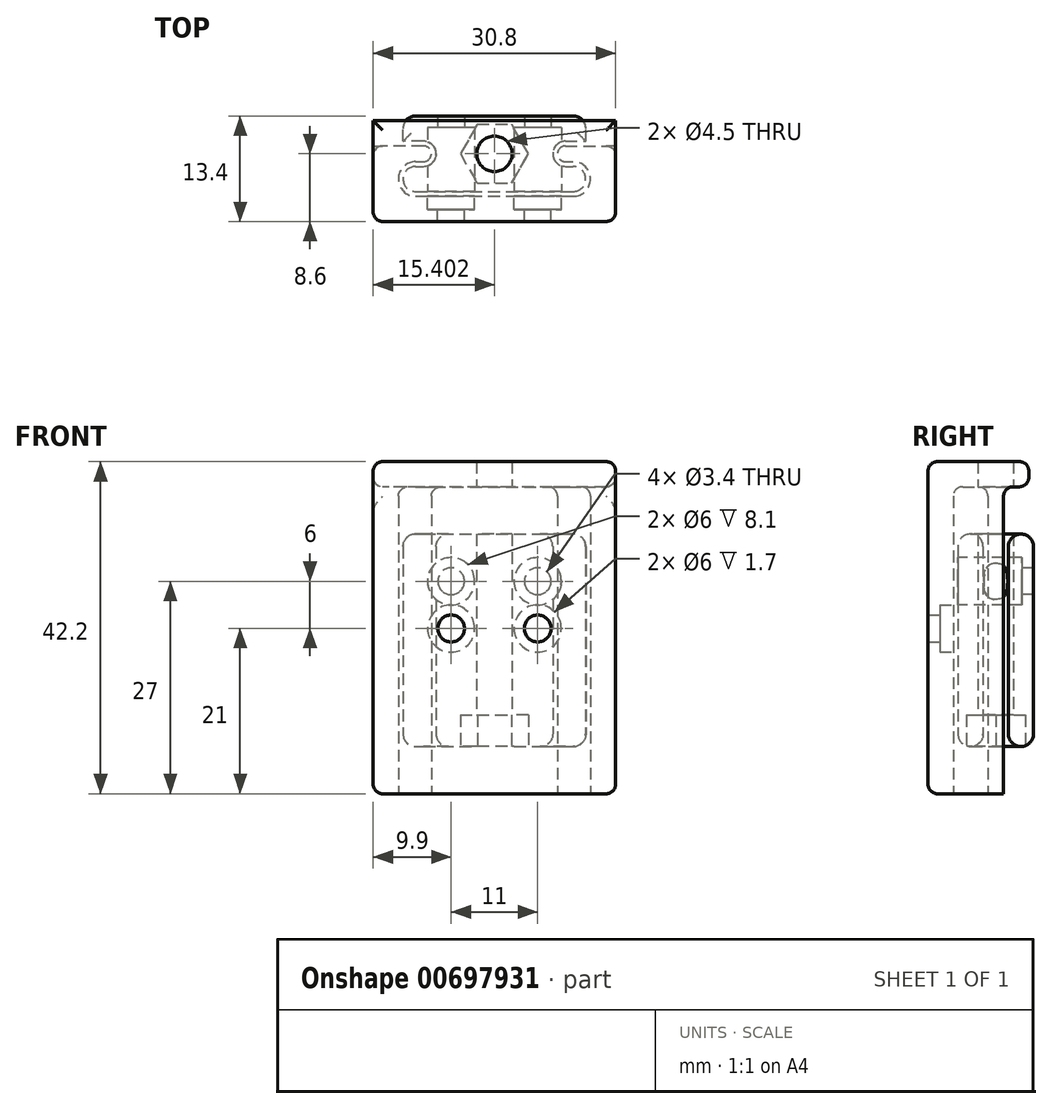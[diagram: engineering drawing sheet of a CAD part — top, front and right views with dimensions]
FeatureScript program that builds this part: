
annotation { "Feature Type Name" : "Feature", "Feature Type Description" : "" }
export const myFeature = defineFeature(function(context is Context, id is Id, definition is map)
    precondition{}
    {
        {
            assignVariable(context, id + "F0", {"name" : "HoleWallD", "anyValue" : 1.5});
        }
        {
            assignVariable(context, id + "F1", {"name" : "RailD", "anyValue" : 3.2});
        }
        {
            assignVariable(context, id + "F2", {"name" : "SliderH", "anyValue" : 21 + 6});
        }
        {
            assignVariable(context, id + "F3", {"name" : "SliderBoltHole", "anyValue" : 4.5});
        }
        {
            assignVariable(context, id + "F4", {"name" : "MountH", "anyValue" : 21 + 6 + 12});
        }
        {
            var Q0;
            Q0=qCreatedBy(makeId("Top.planeOp"),FACE);
            var sketch = newSketch(context, id + "F5", { "sketchPlane" : qUnion([Q0])});
            skArc(sketch, "E0", {"start": v(-9, -0.47) * mm, "mid": v(-7.4, 1.13) * mm, "end": v(-9, 2.73) * mm});
            skLineSegment(sketch, "E1", {"start": v(-9, 2.73) * mm, "end": v(-11.6, 2.73) * mm});
            skLineSegment(sketch, "E2", {"start": v(-11.6, 2.73) * mm, "end": v(-11.6, 5.93) * mm});
            skLineSegment(sketch, "E3", {"start": v(-10, -3.67) * mm, "end": v(0, -3.67) * mm});
            skLineSegment(sketch, "E4", {"start": v(0, 5.93) * mm, "end": v(-11.6, 5.93) * mm});
            skLineSegment(sketch, "E5", {"start": v(-15.4, -7.47) * mm, "end": v(0, -7.47) * mm});
            skLineSegment(sketch, "E6", {"start": v(-10, -0.47) * mm, "end": v(-9, -0.47) * mm});
            skPoint(sketch, "E7", {"position": v(-5.5, 5.93) * mm});
            skPoint(sketch, "E8", {"position": v(-5.5, -7.47) * mm});
            skArc(sketch, "E9", {"start": v(-10, -0.47) * mm, "mid": v(-11.6, -2.07) * mm, "end": v(-10, -3.67) * mm});
            skLineSegment(sketch, "E10.0", {"start": v(-10, -4.27) * mm, "end": v(0, -4.27) * mm});
            skLineSegment(sketch, "E10.1", {"start": v(-9, 2.13) * mm, "end": v(-15.4, 2.13) * mm});
            skArc(sketch, "E10.2", {"start": v(-9, 0.13) * mm, "mid": v(-8, 1.13) * mm, "end": v(-9, 2.13) * mm});
            skLineSegment(sketch, "E10.3", {"start": v(-10, 0.13) * mm, "end": v(-9, 0.13) * mm});
            skArc(sketch, "E10.4", {"start": v(-10, 0.13) * mm, "mid": v(-12.2, -2.07) * mm, "end": v(-10, -4.27) * mm});
            skLineSegment(sketch, "E11", {"start": v(-15.4, 2.13) * mm, "end": v(-15.4, -7.47) * mm});
            skLineSegment(sketch, "E12", {"start": v(0, 5.93) * mm, "end": v(0, 5.93) * mm});
            skLineSegment(sketch, "E13", {"start": v(0, -4.27) * mm, "end": v(0, -7.47) * mm});
            skLineSegment(sketch, "E14.MirrorCS", {"start": v(10, -4.27) * mm, "end": v(0, -4.27) * mm});
            skLineSegment(sketch, "E15.MirrorCS", {"start": v(10, -3.67) * mm, "end": v(0, -3.67) * mm});
            skArc(sketch, "E16.MirrorCS", {"start": v(9, -0.47) * mm, "mid": v(7.4, 1.13) * mm, "end": v(9, 2.73) * mm});
            skLineSegment(sketch, "E17.MirrorCS", {"start": v(9, 2.13) * mm, "end": v(15.4, 2.13) * mm});
            skPoint(sketch, "E18.MirrorP", {"position": v(5.5, 5.93) * mm});
            skLineSegment(sketch, "E19.MirrorCS", {"start": v(15.4, -7.47) * mm, "end": v(0, -7.47) * mm});
            skArc(sketch, "E20.MirrorCS", {"start": v(9, 0.13) * mm, "mid": v(8, 1.13) * mm, "end": v(9, 2.13) * mm});
            skLineSegment(sketch, "E21.MirrorCS", {"start": v(9, 2.73) * mm, "end": v(11.6, 2.73) * mm});
            skLineSegment(sketch, "E22.MirrorCS", {"start": v(9, 0.13) * mm, "end": v(10, 0.13) * mm});
            skLineSegment(sketch, "E23.MirrorCS", {"start": v(0, 5.93) * mm, "end": v(11.6, 5.93) * mm});
            skArc(sketch, "E24.MirrorCS", {"start": v(10, 0.13) * mm, "mid": v(12.2, -2.07) * mm, "end": v(10, -4.27) * mm});
            skLineSegment(sketch, "E25.MirrorCS", {"start": v(11.6, 2.73) * mm, "end": v(11.6, 5.93) * mm});
            skArc(sketch, "E26.MirrorCS", {"start": v(10, -0.47) * mm, "mid": v(11.6, -2.07) * mm, "end": v(10, -3.67) * mm});
            skLineSegment(sketch, "E27.MirrorCS", {"start": v(9, -0.47) * mm, "end": v(10, -0.47) * mm});
            skLineSegment(sketch, "E28.MirrorCS", {"start": v(15.4, 2.13) * mm, "end": v(15.4, -7.47) * mm});
            skPoint(sketch, "E29.MirrorP", {"position": v(5.5, -7.47) * mm});
            skSolve(sketch);
        }
        {
            var Q0;
            Q0=makeQuery(id+"F5.imprint","IMPRINT",FACE,{"disambiguationData":[TD([[makeQuery(id+"F5.imprint","IMPRINT",EDGE,{"derivedFrom":sQuery(id+"F5.wireOp",EDGE,"E0")}),-1.0]])]});
            var Q1;
            {var subQ1=sQuery(id+"F5.wireOp",EDGE,"E15.MirrorCS");Q1=makeQuery(id+"F5.imprint","IMPRINT",FACE,{"disambiguationData":[TD([[makeQuery(id+"F5.imprint","IMPRINT",EDGE,{"derivedFrom":subQ1}),-1.0]])]});}
            extrude(context, id + "F6", {"entities" : qUnion([Q0, Q1]), "endBound" : BoundingType.SYMMETRIC, "depth" : (getVariable(context, 'SliderH')) * mm, "offsetDistance" : 25 * mm});
        }
        {
            var Q0;
            Q0=makeQuery(id+"F6.opExtrude","SWEPT_EDGE",EDGE,{"disambiguationData":[OSD([sQuery(id+"F5.wireOp",EDGE,"E2"),sQuery(id+"F5.wireOp",EDGE,"E4")])]});
            var Q1;
            Q1=makeQuery(id+"F6.opExtrude","SWEPT_EDGE",EDGE,{"disambiguationData":[OSD([sQuery(id+"F5.wireOp",EDGE,"E23.MirrorCS"),sQuery(id+"F5.wireOp",EDGE,"E25.MirrorCS")])]});
            var Q2;
            Q2=makeQuery(id+"F6.opExtrude","CAP_FACE",FACE,{"disambiguationData":[OSD([sQuery(id+"F5.wireOp",EDGE,"E0"),sQuery(id+"F5.wireOp",EDGE,"E1"),sQuery(id+"F5.wireOp",EDGE,"E2"),sQuery(id+"F5.wireOp",EDGE,"E3"),sQuery(id+"F5.wireOp",EDGE,"E4"),sQuery(id+"F5.wireOp",EDGE,"E6"),sQuery(id+"F5.wireOp",EDGE,"E9"),sQuery(id+"F5.wireOp",EDGE,"E15.MirrorCS"),sQuery(id+"F5.wireOp",EDGE,"E16.MirrorCS"),sQuery(id+"F5.wireOp",EDGE,"E21.MirrorCS"),sQuery(id+"F5.wireOp",EDGE,"E23.MirrorCS"),sQuery(id+"F5.wireOp",EDGE,"E25.MirrorCS"),sQuery(id+"F5.wireOp",EDGE,"E26.MirrorCS"),sQuery(id+"F5.wireOp",EDGE,"E27.MirrorCS")])],"isStart":true});
            var Q3;
            Q3=makeQuery(id+"F6.opExtrude","CAP_FACE",FACE,{"disambiguationData":[OSD([sQuery(id+"F5.wireOp",EDGE,"E0"),sQuery(id+"F5.wireOp",EDGE,"E1"),sQuery(id+"F5.wireOp",EDGE,"E2"),sQuery(id+"F5.wireOp",EDGE,"E3"),sQuery(id+"F5.wireOp",EDGE,"E4"),sQuery(id+"F5.wireOp",EDGE,"E6"),sQuery(id+"F5.wireOp",EDGE,"E9"),sQuery(id+"F5.wireOp",EDGE,"E15.MirrorCS"),sQuery(id+"F5.wireOp",EDGE,"E16.MirrorCS"),sQuery(id+"F5.wireOp",EDGE,"E21.MirrorCS"),sQuery(id+"F5.wireOp",EDGE,"E23.MirrorCS"),sQuery(id+"F5.wireOp",EDGE,"E25.MirrorCS"),sQuery(id+"F5.wireOp",EDGE,"E26.MirrorCS"),sQuery(id+"F5.wireOp",EDGE,"E27.MirrorCS")])],"isStart":false});
            fillet(context, id + "F7", {"entities" : qUnion([Q0, Q1, Q2, Q3]), "radius" : 1.6 * mm, "tangentPropagation" : true, "allowEdgeOverflow" : false});
        }
        {
            var Q0;
            Q0=makeQuery(id+"F6.opExtrude","SWEPT_FACE",FACE,{"disambiguationData":[OSD([sQuery(id+"F5.wireOp",EDGE,"E3"),sQuery(id+"F5.wireOp",EDGE,"E15.MirrorCS")])]});
            var sketch = newSketch(context, id + "F8", { "sketchPlane" : qUnion([Q0])});
            skLineSegment(sketch, "E30.bottom", {"start": v(5.5, 7.5) * mm, "end": v(-5.5, 7.5) * mm});
            skLineSegment(sketch, "E30.top", {"start": v(5.5, -7.5) * mm, "end": v(-5.5, -7.5) * mm});
            skLineSegment(sketch, "E30.left", {"start": v(5.5, 7.5) * mm, "end": v(5.5, -7.5) * mm});
            skLineSegment(sketch, "E30.right", {"start": v(-5.5, 7.5) * mm, "end": v(-5.5, -7.5) * mm});
            skPoint(sketch, "E30.middle", {"position": v(0, 0) * mm});
            skSolve(sketch);
        }
        {
            var Q0;
            Q0=makeQuery(id+"F6.opExtrude","CAP_FACE",FACE,{"disambiguationData":[OSD([sQuery(id+"F5.wireOp",EDGE,"E0"),sQuery(id+"F5.wireOp",EDGE,"E1"),sQuery(id+"F5.wireOp",EDGE,"E2"),sQuery(id+"F5.wireOp",EDGE,"E3"),sQuery(id+"F5.wireOp",EDGE,"E4"),sQuery(id+"F5.wireOp",EDGE,"E6"),sQuery(id+"F5.wireOp",EDGE,"E9"),sQuery(id+"F5.wireOp",EDGE,"E12"),sQuery(id+"F5.wireOp",EDGE,"E15.MirrorCS"),sQuery(id+"F5.wireOp",EDGE,"E16.MirrorCS"),sQuery(id+"F5.wireOp",EDGE,"E12"),sQuery(id+"F5.wireOp",EDGE,"E21.MirrorCS"),sQuery(id+"F5.wireOp",EDGE,"E23.MirrorCS"),sQuery(id+"F5.wireOp",EDGE,"E25.MirrorCS"),sQuery(id+"F5.wireOp",EDGE,"E26.MirrorCS"),sQuery(id+"F5.wireOp",EDGE,"E27.MirrorCS")])],"isStart":true});
            var sketch = newSketch(context, id + "F9", { "sketchPlane" : qUnion([Q0])});
            skPoint(sketch, "E31", {"position": v(0, 0) * mm});
            skCircle(sketch, "E32.cCircle", {"center": v(0, -1.13) * mm, "radius": 3.75 * mm, "construction": true});
            skLineSegment(sketch, "E32.0", {"start": v(4.33, -1.13) * mm, "end": v(2.17, -4.88) * mm});
            skLineSegment(sketch, "E32.1", {"start": v(2.17, -4.88) * mm, "end": v(-2.16, -4.88) * mm});
            skLineSegment(sketch, "E32.2", {"start": v(-2.16, -4.88) * mm, "end": v(-4.33, -1.13) * mm});
            skLineSegment(sketch, "E32.3", {"start": v(-4.33, -1.13) * mm, "end": v(-2.16, 2.62) * mm});
            skLineSegment(sketch, "E32.4", {"start": v(-2.16, 2.62) * mm, "end": v(2.17, 2.62) * mm});
            skLineSegment(sketch, "E32.5", {"start": v(2.17, 2.62) * mm, "end": v(4.33, -1.13) * mm});
            skPoint(sketch, "E32.0.midPoint", {"position": v(3.25, -3) * mm});
            skSolve(sketch);
        }
        {
            var Q0;
            Q0=sQuery(id+"F8.wireOp",VERTEX,"E30.right.start");
            var Q1;
            Q1=sQuery(id+"F8.wireOp",VERTEX,"E30.left.start");
            var Q2;
            Q2=makeQuery(id+"F6.opExtrude","SWEPT_BODY",BODY,{"disambiguationData":[OSD([sQuery(id+"F5.wireOp",EDGE,"E0"),sQuery(id+"F5.wireOp",EDGE,"E1"),sQuery(id+"F5.wireOp",EDGE,"E2"),sQuery(id+"F5.wireOp",EDGE,"E3"),sQuery(id+"F5.wireOp",EDGE,"E4"),sQuery(id+"F5.wireOp",EDGE,"E6"),sQuery(id+"F5.wireOp",EDGE,"E9"),sQuery(id+"F5.wireOp",EDGE,"E12"),sQuery(id+"F5.wireOp",EDGE,"E15.MirrorCS"),sQuery(id+"F5.wireOp",EDGE,"E16.MirrorCS"),sQuery(id+"F5.wireOp",EDGE,"E12"),sQuery(id+"F5.wireOp",EDGE,"E21.MirrorCS"),sQuery(id+"F5.wireOp",EDGE,"E23.MirrorCS"),sQuery(id+"F5.wireOp",EDGE,"E25.MirrorCS"),sQuery(id+"F5.wireOp",EDGE,"E26.MirrorCS"),sQuery(id+"F5.wireOp",EDGE,"E27.MirrorCS")])]});
            hole(context, id + "F10", {"style" : HoleStyle.C_BORE, "endStyle" : HoleEndStyle.THROUGH, "holeDiameter" : 3.4 * mm, "cBoreDiameter" : 6 * mm, "cBoreDepth" : ((getVariable(context, 'RailD') * 3) - getVariable(context, 'HoleWallD')) * mm, "majorDiameter" : 5 * mm, "isTappedThrough" : true, "tappedDepth" : 12 * mm, "tapClearance" : 3, "locations" : qUnion([Q0, Q1]), "scope" : qUnion([Q2])});
        }
        {
            var Q0;
            {var subQ4=sQuery(id+"F9.wireOp",EDGE,"E32.2");Q0=makeQuery(id+"F9.imprint","IMPRINT",FACE,{"disambiguationData":[TD([[makeQuery(id+"F9.imprint","IMPRINT",EDGE,{"derivedFrom":subQ4}),-1.0]])]});}
            var Q1;
            {var subQ5=sQuery(id+"F9.wireOp",EDGE,"E32.0");Q1=makeQuery(id+"F9.imprint","IMPRINT",FACE,{"disambiguationData":[TD([[makeQuery(id+"F9.imprint","IMPRINT",EDGE,{"derivedFrom":subQ5}),-1.0]])]});}
            var Q2;
            {var subQ0=sQuery(id+"F9.wireOp",EDGE,"E32.4");Q2=makeQuery(id+"F9.imprint","IMPRINT",FACE,{"disambiguationData":[TD([[makeQuery(id+"F9.imprint","IMPRINT",EDGE,{"derivedFrom":subQ0}),-1.0]])]});}
            var Q3;
            {var subQ0=sQuery(id+"F9.wireOp",EDGE,"E32.5");var subQ1=sQuery(id+"F9.wireOp",EDGE,"E32.0");var subQ2=makeQuery(id+"F9.imprint","INTERSECT",VERTEX,{"derivedFrom":[subQ1,subQ0]});Q3=makeQuery(id+"F9.imprint","IMPRINT",FACE,{"disambiguationData":[TD([[makeQuery(id+"F9.imprint","IMPRINT",EDGE,{"disambiguationData":[TD([[subQ2,-1.0]])],"derivedFrom":subQ1}),-1.0]])]});}
            extrude(context, id + "F11", {"entities" : qUnion([Q0, Q1, Q2, Q3]), "operationType" : NewBodyOperationType.REMOVE, "oppositeDirection" : true, "depth" : 4 * mm, "offsetDistance" : 25 * mm});
        }
        {
            var Q0;
            Q0=sQuery(id+"F9.wireOp",VERTEX,"E32.cCircle.center");
            var Q1;
            Q1=makeQuery(id+"F6.opExtrude","SWEPT_BODY",BODY,{"disambiguationData":[OSD([sQuery(id+"F5.wireOp",EDGE,"E0"),sQuery(id+"F5.wireOp",EDGE,"E1"),sQuery(id+"F5.wireOp",EDGE,"E2"),sQuery(id+"F5.wireOp",EDGE,"E3"),sQuery(id+"F5.wireOp",EDGE,"E4"),sQuery(id+"F5.wireOp",EDGE,"E6"),sQuery(id+"F5.wireOp",EDGE,"E9"),sQuery(id+"F5.wireOp",EDGE,"E12"),sQuery(id+"F5.wireOp",EDGE,"E15.MirrorCS"),sQuery(id+"F5.wireOp",EDGE,"E16.MirrorCS"),sQuery(id+"F5.wireOp",EDGE,"E12"),sQuery(id+"F5.wireOp",EDGE,"E21.MirrorCS"),sQuery(id+"F5.wireOp",EDGE,"E23.MirrorCS"),sQuery(id+"F5.wireOp",EDGE,"E25.MirrorCS"),sQuery(id+"F5.wireOp",EDGE,"E26.MirrorCS"),sQuery(id+"F5.wireOp",EDGE,"E27.MirrorCS")])]});
            hole(context, id + "F12", {"style" : HoleStyle.SIMPLE, "endStyle" : HoleEndStyle.THROUGH, "holeDiameter" : (getVariable(context, 'SliderBoltHole')) * mm, "majorDiameter" : 5 * mm, "isTappedThrough" : true, "tappedDepth" : 12 * mm, "tapClearance" : 3, "locations" : qUnion([Q0]), "scope" : qUnion([Q1])});
        }
        {
            var Q0;
            Q0=makeQuery(id+"F5.imprint","IMPRINT",FACE,{"disambiguationData":[TD([[makeQuery(id+"F5.imprint","IMPRINT",EDGE,{"derivedFrom":sQuery(id+"F5.wireOp",EDGE,"E5")}),1.0]])]});
            var Q1;
            Q1=makeQuery(id+"F5.imprint","IMPRINT",FACE,{"disambiguationData":[TD([[makeQuery(id+"F5.imprint","IMPRINT",EDGE,{"derivedFrom":sQuery(id+"F5.wireOp",EDGE,"E14.MirrorCS")}),1.0]])]});
            extrude(context, id + "F13", {"entities" : qUnion([Q0, Q1]), "endBound" : BoundingType.SYMMETRIC, "depth" : (getVariable(context, 'MountH')) * mm, "offsetDistance" : 25 * mm});
        }
        {
            var Q0;
            Q0=makeQuery(id+"F13.opExtrude","SWEPT_FACE",FACE,{"disambiguationData":[OSD([sQuery(id+"F5.wireOp",EDGE,"E10.0"),sQuery(id+"F5.wireOp",EDGE,"E14.MirrorCS")])]});
            var sketch = newSketch(context, id + "F14", { "sketchPlane" : qUnion([Q0])});
            skLineSegment(sketch, "E33.bottom", {"start": v(-5.5, 1.5) * mm, "end": v(5.5, 1.5) * mm});
            skLineSegment(sketch, "E33.top", {"start": v(5.5, -1.5) * mm, "end": v(-5.5, -1.5) * mm});
            skLineSegment(sketch, "E33.left", {"start": v(-5.5, 1.5) * mm, "end": v(-5.5, -1.5) * mm});
            skLineSegment(sketch, "E33.right", {"start": v(5.5, 1.5) * mm, "end": v(5.5, -1.5) * mm});
            skPoint(sketch, "E33.middle", {"position": v(0, 0) * mm});
            skSolve(sketch);
        }
        {
            var Q0;
            Q0=sQuery(id+"F14.wireOp",VERTEX,"E33.bottom.start");
            var Q1;
            Q1=sQuery(id+"F14.wireOp",VERTEX,"E33.right.start");
            var Q2;
            Q2=makeQuery(id+"F13.opExtrude","SWEPT_BODY",BODY,{"disambiguationData":[OSD([sQuery(id+"F5.wireOp",EDGE,"E5"),sQuery(id+"F5.wireOp",EDGE,"E10.0"),sQuery(id+"F5.wireOp",EDGE,"E10.1"),sQuery(id+"F5.wireOp",EDGE,"E10.2"),sQuery(id+"F5.wireOp",EDGE,"E10.3"),sQuery(id+"F5.wireOp",EDGE,"E10.4"),sQuery(id+"F5.wireOp",EDGE,"E11"),sQuery(id+"F5.wireOp",EDGE,"E14.MirrorCS"),sQuery(id+"F5.wireOp",EDGE,"E17.MirrorCS"),sQuery(id+"F5.wireOp",EDGE,"E19.MirrorCS"),sQuery(id+"F5.wireOp",EDGE,"E20.MirrorCS"),sQuery(id+"F5.wireOp",EDGE,"E22.MirrorCS"),sQuery(id+"F5.wireOp",EDGE,"E24.MirrorCS"),sQuery(id+"F5.wireOp",EDGE,"E28.MirrorCS")])]});
            hole(context, id + "F15", {"style" : HoleStyle.C_BORE, "endStyle" : HoleEndStyle.THROUGH, "holeDiameter" : 3.4 * mm, "cBoreDiameter" : 6 * mm, "cBoreDepth" : (getVariable(context, 'RailD') - getVariable(context, 'HoleWallD')) * mm, "majorDiameter" : 5 * mm, "isTappedThrough" : true, "tappedDepth" : 12 * mm, "tapClearance" : 3, "locations" : qUnion([Q0, Q1]), "scope" : qUnion([Q2])});
        }
        {
            var Q0;
            Q0=makeQuery(id+"F13.opExtrude","CAP_FACE",FACE,{"disambiguationData":[OSD([sQuery(id+"F5.wireOp",EDGE,"E5"),sQuery(id+"F5.wireOp",EDGE,"E10.0"),sQuery(id+"F5.wireOp",EDGE,"E10.1"),sQuery(id+"F5.wireOp",EDGE,"E10.2"),sQuery(id+"F5.wireOp",EDGE,"E10.3"),sQuery(id+"F5.wireOp",EDGE,"E10.4"),sQuery(id+"F5.wireOp",EDGE,"E11"),sQuery(id+"F5.wireOp",EDGE,"E14.MirrorCS"),sQuery(id+"F5.wireOp",EDGE,"E17.MirrorCS"),sQuery(id+"F5.wireOp",EDGE,"E19.MirrorCS"),sQuery(id+"F5.wireOp",EDGE,"E20.MirrorCS"),sQuery(id+"F5.wireOp",EDGE,"E22.MirrorCS"),sQuery(id+"F5.wireOp",EDGE,"E24.MirrorCS"),sQuery(id+"F5.wireOp",EDGE,"E28.MirrorCS")])],"isStart":false});
            var sketch = newSketch(context, id + "F16", { "sketchPlane" : qUnion([Q0])});
            skLineSegment(sketch, "E34.bottom", {"start": v(15.4, -7.47) * mm, "end": v(-15.4, -7.47) * mm});
            skLineSegment(sketch, "E34.top", {"start": v(15.4, 5.33) * mm, "end": v(-15.4, 5.33) * mm});
            skLineSegment(sketch, "E34.left", {"start": v(15.4, -7.47) * mm, "end": v(15.4, 5.33) * mm});
            skLineSegment(sketch, "E34.right", {"start": v(-15.4, -7.47) * mm, "end": v(-15.4, 5.33) * mm});
            skSolve(sketch);
        }
        {
            var Q0;
            Q0 = qSketchRegion(id + "F16", true);
            extrude(context, id + "F17", {"entities" : qUnion([Q0]), "operationType" : NewBodyOperationType.ADD, "depth" : (getVariable(context, 'RailD')) * mm, "offsetDistance" : 25 * mm});
        }
        {
            var Q0;
            Q0=makeQuery(id+"F17.opExtrude","CAP_FACE",FACE,{"disambiguationData":[OSD([sQuery(id+"F16.wireOp",EDGE,"E34.bottom"),sQuery(id+"F16.wireOp",EDGE,"E34.top"),sQuery(id+"F16.wireOp",EDGE,"E34.left"),sQuery(id+"F16.wireOp",EDGE,"E34.right")])],"isStart":false});
            var Q1;
            Q1=makeQuery(id+"F17.opExtrude","CAP_FACE",FACE,{"disambiguationData":[OSD([sQuery(id+"F16.wireOp",EDGE,"E34.bottom"),sQuery(id+"F16.wireOp",EDGE,"E34.top"),sQuery(id+"F16.wireOp",EDGE,"E34.left"),sQuery(id+"F16.wireOp",EDGE,"E34.right")])],"isStart":true});
            var Q2;
            Q2=makeQuery(id+"F17.boolean.opBoolean","MERGE",EDGE,{"derivedFrom":[makeQuery(id+"F13.opExtrude","SWEPT_EDGE",EDGE,{"disambiguationData":[OSD([sQuery(id+"F5.wireOp",EDGE,"E19.MirrorCS"),sQuery(id+"F5.wireOp",EDGE,"E28.MirrorCS")])]}),makeQuery(id+"F17.opExtrude","SWEPT_EDGE",EDGE,{"disambiguationData":[OSD([sQuery(id+"F16.wireOp",EDGE,"E34.bottom"),sQuery(id+"F16.wireOp",EDGE,"E34.left")])]})]});
            var Q3;
            Q3=makeQuery(id+"F17.boolean.opBoolean","MERGE",EDGE,{"derivedFrom":[makeQuery(id+"F13.opExtrude","SWEPT_EDGE",EDGE,{"disambiguationData":[OSD([sQuery(id+"F5.wireOp",EDGE,"E5"),sQuery(id+"F5.wireOp",EDGE,"E11")])]}),makeQuery(id+"F17.opExtrude","SWEPT_EDGE",EDGE,{"disambiguationData":[OSD([sQuery(id+"F16.wireOp",EDGE,"E34.bottom"),sQuery(id+"F16.wireOp",EDGE,"E34.right")])]})]});
            var Q4;
            Q4=makeQuery(id+"F13.opExtrude","CAP_EDGE",EDGE,{"disambiguationData":[OSD([sQuery(id+"F5.wireOp",EDGE,"E5"),sQuery(id+"F5.wireOp",EDGE,"E19.MirrorCS")])],"isStart":true});
            var Q5;
            Q5=makeQuery(id+"F13.opExtrude","CAP_EDGE",EDGE,{"disambiguationData":[OSD([sQuery(id+"F5.wireOp",EDGE,"E28.MirrorCS")])],"isStart":true});
            var Q6;
            Q6=makeQuery(id+"F13.opExtrude","CAP_EDGE",EDGE,{"disambiguationData":[OSD([sQuery(id+"F5.wireOp",EDGE,"E11")])],"isStart":true});
            fillet(context, id + "F18", {"entities" : qUnion([Q0, Q1, Q2, Q3, Q4, Q5, Q6]), "radius" : 1.2 * mm, "tangentPropagation" : true, "allowEdgeOverflow" : false});
        }
        {
            var Q0;
            Q0=sQuery(id+"F9.wireOp",VERTEX,"E32.cCircle.center");
            var Q1;
            Q1=makeQuery(id+"F13.opExtrude","SWEPT_BODY",BODY,{"disambiguationData":[OSD([sQuery(id+"F5.wireOp",EDGE,"E5"),sQuery(id+"F5.wireOp",EDGE,"E10.0"),sQuery(id+"F5.wireOp",EDGE,"E10.1"),sQuery(id+"F5.wireOp",EDGE,"E10.2"),sQuery(id+"F5.wireOp",EDGE,"E10.3"),sQuery(id+"F5.wireOp",EDGE,"E10.4"),sQuery(id+"F5.wireOp",EDGE,"E11"),sQuery(id+"F5.wireOp",EDGE,"E14.MirrorCS"),sQuery(id+"F5.wireOp",EDGE,"E17.MirrorCS"),sQuery(id+"F5.wireOp",EDGE,"E19.MirrorCS"),sQuery(id+"F5.wireOp",EDGE,"E20.MirrorCS"),sQuery(id+"F5.wireOp",EDGE,"E22.MirrorCS"),sQuery(id+"F5.wireOp",EDGE,"E24.MirrorCS"),sQuery(id+"F5.wireOp",EDGE,"E28.MirrorCS")])]});
            hole(context, id + "F19", {"style" : HoleStyle.SIMPLE, "endStyle" : HoleEndStyle.THROUGH, "holeDiameter" : (getVariable(context, 'SliderBoltHole')) * mm, "majorDiameter" : 5 * mm, "isTappedThrough" : true, "tappedDepth" : 12 * mm, "tapClearance" : 3, "locations" : qUnion([Q0]), "scope" : qUnion([Q1])});
        }
    });
